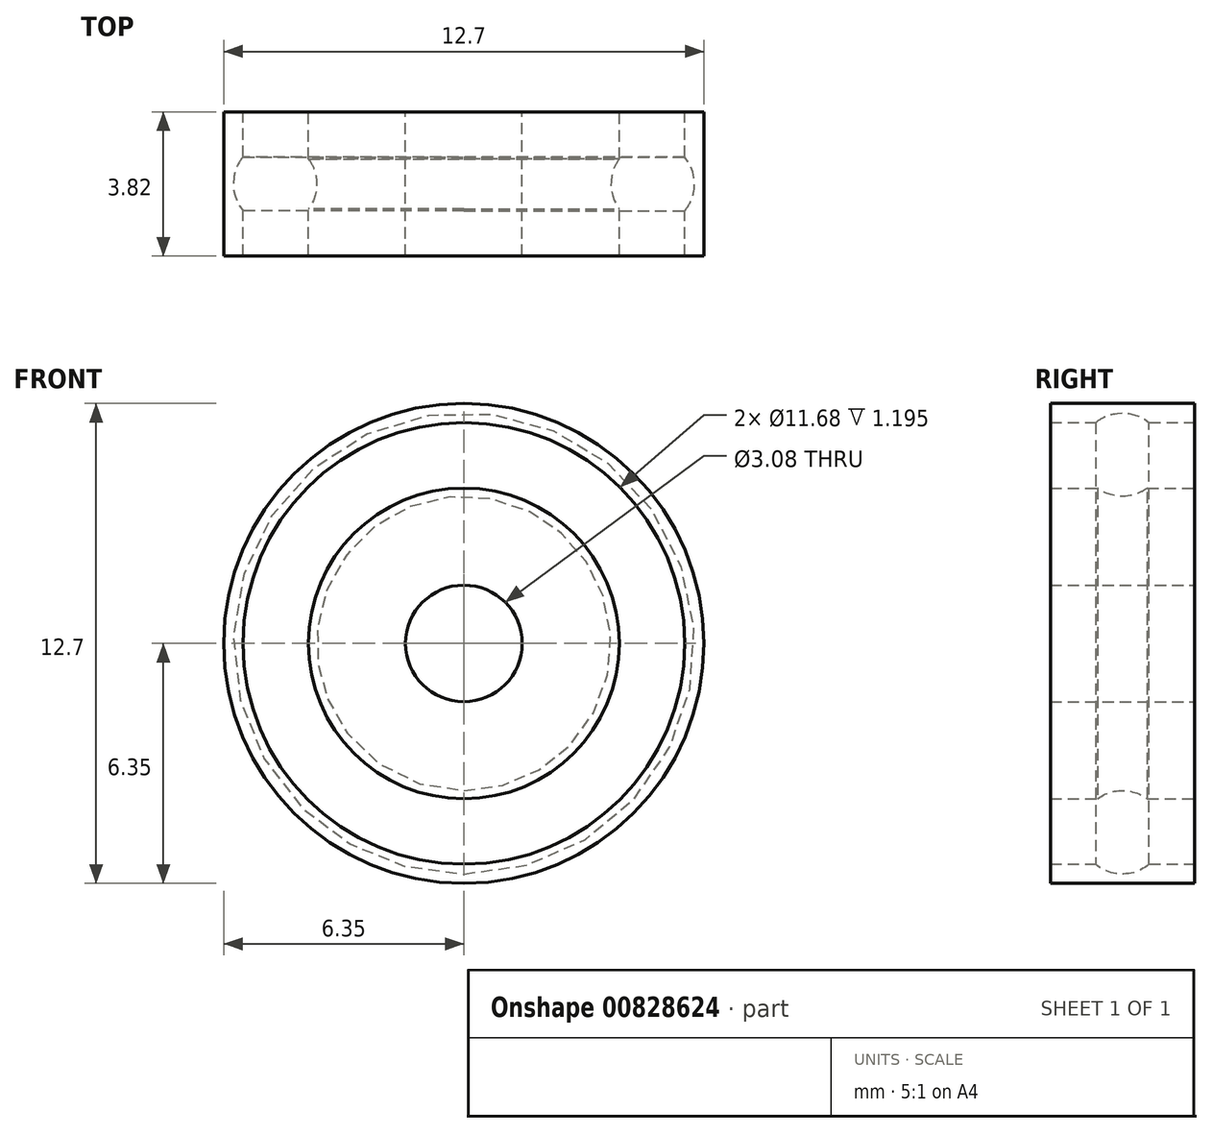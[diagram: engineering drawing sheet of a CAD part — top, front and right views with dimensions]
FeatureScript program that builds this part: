
annotation { "Feature Type Name" : "Feature", "Feature Type Description" : "" }
export const myFeature = defineFeature(function(context is Context, id is Id, definition is map)
    precondition{}
    {
        {
            var Q0;
            Q0=qCreatedBy(makeId("Front.planeOp"),FACE);
            var sketch = newSketch(context, id + "F0", { "sketchPlane" : qUnion([Q0])});
            skCircle(sketch, "E0", {"center": v(0, 0) * mm, "radius": 6.35 * mm});
            skCircle(sketch, "E1", {"center": v(0, 0) * mm, "radius": 5.84 * mm});
            skCircle(sketch, "E2", {"center": v(0, 0) * mm, "radius": 4.11 * mm});
            skCircle(sketch, "E3", {"center": v(0, 0) * mm, "radius": 1.54 * mm});
            skSolve(sketch);
        }
        {
            var Q0;
            Q0 = qSketchRegion(id + "F0", true);
            var Q1;
            Q1=makeQuery(id+"F0.imprint","IMPRINT",FACE,{"disambiguationData":[TD([[makeQuery(id+"F0.imprint","IMPRINT",EDGE,{"derivedFrom":sQuery(id+"F0.wireOp",EDGE,"E2")}),1.0]])]});
            extrude(context, id + "F1", {"entities" : qUnion([Q0, Q1]), "endBound" : BoundingType.SYMMETRIC, "depth" : 3.8 * mm, "offsetDistance" : 25.4 * mm});
        }
        {
            var Q0;
            Q0=qCreatedBy(makeId("Right.planeOp"),FACE);
            var sketch = newSketch(context, id + "F2", { "sketchPlane" : qUnion([Q0])});
            skCircle(sketch, "E4", {"center": v(0, 5) * mm, "radius": 1.1 * mm});
            skSolve(sketch);
        }
        {
            var Q0;
            Q0=makeQuery(id+"F2.imprint","IMPRINT",FACE,{"disambiguationData":[TD([[makeQuery(id+"F2.imprint","IMPRINT",EDGE,{"derivedFrom":sQuery(id+"F2.wireOp",EDGE,"E4")}),1.0]])]});
            var Q1;
            Q1=makeQuery(id+"F1.opExtrude","CAP_EDGE",EDGE,{"disambiguationData":[OSD([sQuery(id+"F0.wireOp",EDGE,"E2")])],"isStart":false});
            revolve(context, id + "F3", {"operationType" : NewBodyOperationType.REMOVE, "surfaceOperationType" : NewSurfaceOperationType.NEW, "entities" : qUnion([Q0]), "axis" : qUnion([Q1]), "revolveType" : RevolveType.FULL, "oppositeDirection" : true});
        }
    });
